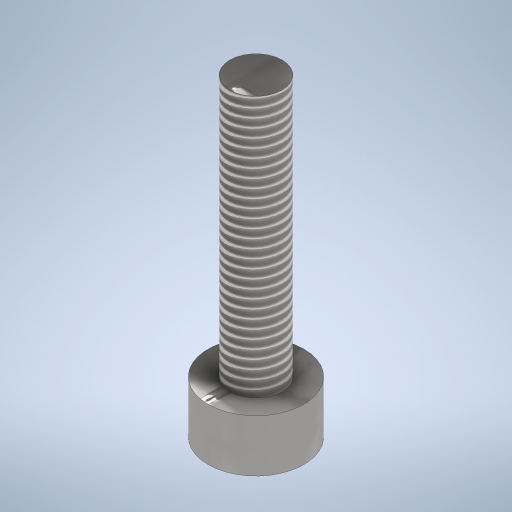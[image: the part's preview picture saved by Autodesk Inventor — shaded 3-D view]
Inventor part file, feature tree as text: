
AUTODESK INVENTOR PART (.ipt)
format: ipt  version: 2024.2 (Build 282272000, 272)  size: 314,368 bytes
history: native  units: mm
features: sketch x2, revolve x1, thread x1, extrude x1
ambient origin geometry x8: Origin, YZ Plane, XZ Plane, XY Plane, X Axis, Y Axis, Z Axis, Center Point
bodies: Solid1 (feature_tree)
feature tree (5):
  revolve  "Revolution1"  [1 undecoded]
  thread  "Thread1"  [1 undecoded]
  extrude  "Extrusion1"  [1 undecoded]
  sketch  "Sketch1"  dims[d4=90.0deg d5=6.0mm d6=0.0mm d0=0.0mm]
  sketch  "Sketch2"
note: 3 required parameter values undecoded (feature->parameter linkage not recoverable at this tier; creation-order binding heuristic only, values carry confidence <= 0.55)